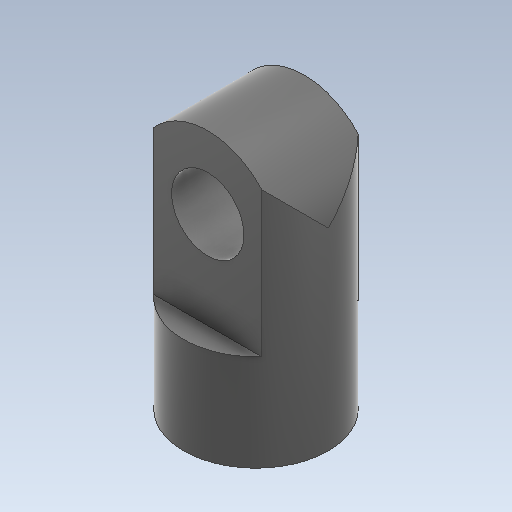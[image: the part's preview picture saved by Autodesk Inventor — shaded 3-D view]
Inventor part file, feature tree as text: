
AUTODESK INVENTOR PART (.ipt)
format: ipt  version: 2020 (Build 240168000, 168)  size: 133,120 bytes
history: native  units: mm
features: extrude x3, sketch x2
ambient origin geometry x8: Origin, YZ Plane, XZ Plane, XY Plane, X Axis, Y Axis, Z Axis, Center Point
bodies: Body1 (feature_tree)
feature tree (5):
  extrude  "押し出し3"  Depth=3.0mm
  sketch  "スケッチ4"
  extrude  "押し出し4"  Depth=6.0mm
  extrude  "押し出し5"  Depth=4.0mm
  sketch  "スケッチ3"
